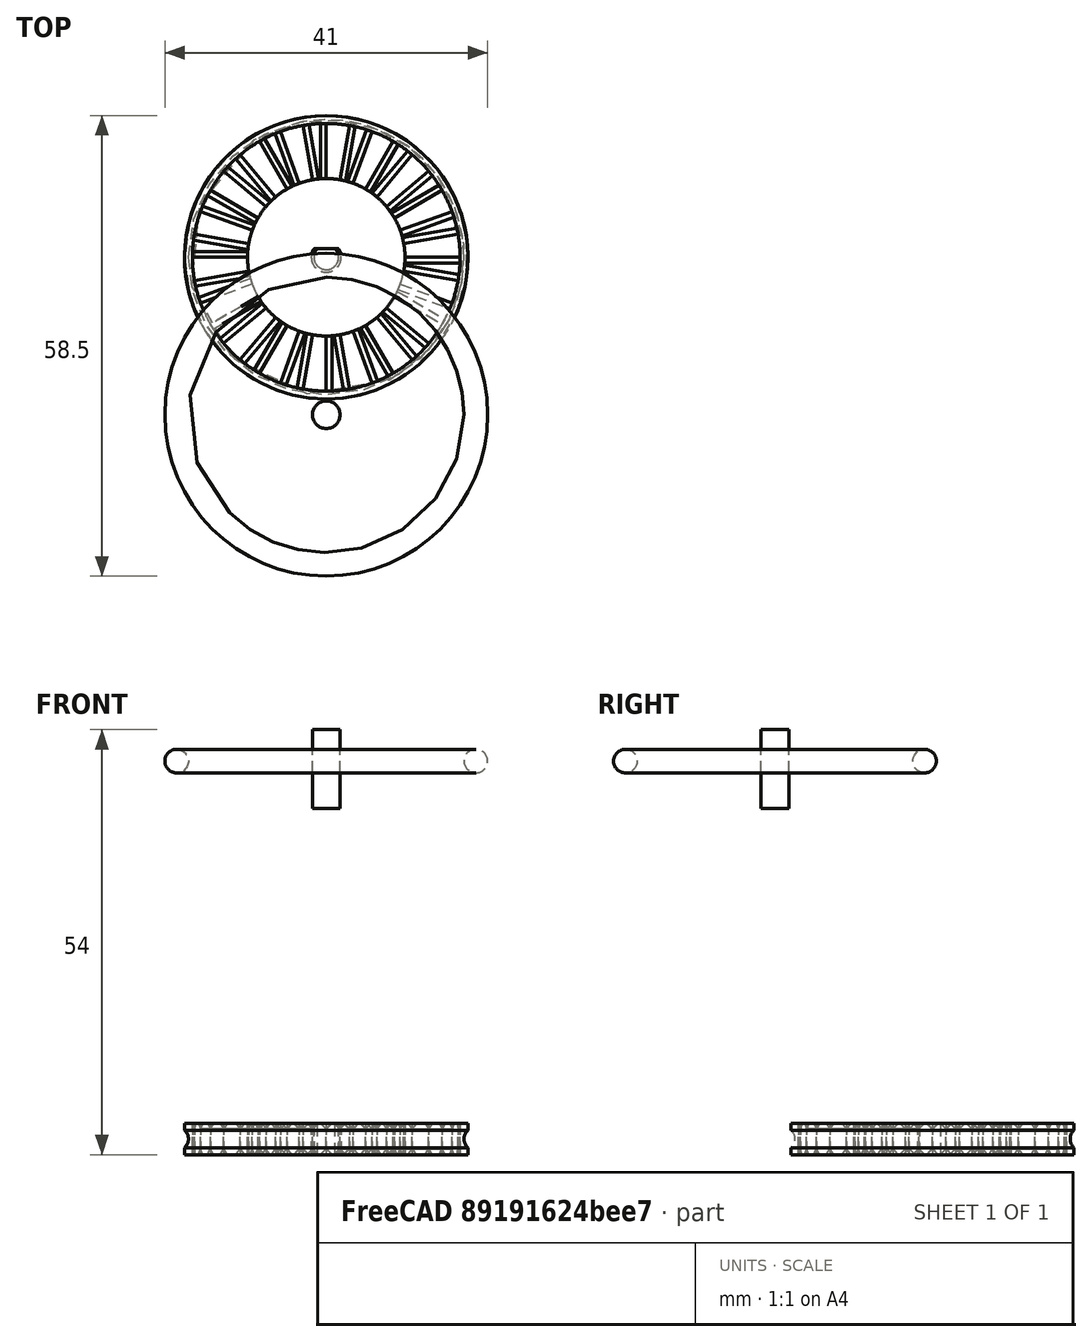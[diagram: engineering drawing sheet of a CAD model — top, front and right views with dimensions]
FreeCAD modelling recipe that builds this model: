
FCSTD DOCUMENT  (FreeCAD 0.17R13522 (Git))
Label: wheel 1.57 hole
License: All rights reserved
LicenseURL: http://en.wikipedia.org/wiki/All_rights_reserved
objects: Part::Feature×34, Part::Cut×13, Part::Cylinder×7, Part::Box×5, Part::Chamfer×4, Part::Torus×3, Part::MultiFuse×2
note: 68 computed .brp shape members not serialized (recipe doc carries the construction recipe); baked Part::Feature solids carry a one-line shape summary decoded from their .brp

FEATURE [Part::Cylinder] Cylinder012  label="wheel1a"
  Angle = 360
  AttacherType = Attacher::AttachEngine3D
  Height = 4
  Radius = 18
FEATURE [Part::Cylinder] Cylinder028  label="Cylinder024"
  Angle = 360
  AttacherType = Attacher::AttachEngine3D
  Height = 10
  Placement = pos=(0,0,-1) rot=(0,0,1;0rad)
  Radius = 1.57
FEATURE [Part::Box] Box084016  label="Cube067"
  AttacherType = Attacher::AttachEngine3D
  Height = 12
  Length = 10
  Placement = pos=(-5,1.1,-1.5) rot=(0,0,1;0rad)
  Width = 10
FEATURE [Part::Cut] Cut057
  Base = -> Cylinder028
  Tool = -> Box084016
FEATURE [Part::Cut] Cut062
  Base = -> Cylinder012
  Tool = -> Cut057
FEATURE [Part::Torus] Torus002
  Angle1 = -180
  Angle2 = 180
  Angle3 = 360
  AttacherType = Attacher::AttachEngine3D
  Placement = pos=(0,0,2) rot=(0,0,1;0rad)
  Radius1 = 19
  Radius2 = 1.5
FEATURE [Part::Cut] Cut063  label="wheel"
  Base = -> Cut062
  Tool = -> Torus002
FEATURE [Part::Torus] Torus
  Angle1 = -180
  Angle2 = 180
  Angle3 = 360
  AttacherType = Attacher::AttachEngine3D
  Placement = pos=(0,-20,50) rot=(0,0,1;0rad)
  Radius1 = 19
  Radius2 = 1.5
FEATURE [Part::Cylinder] Cylinder062  label="Cylinder158"
  Angle = 360
  AttacherType = Attacher::AttachEngine3D
  Height = 10
  Radius = 17
FEATURE [Part::Cylinder] Cylinder063  label="Cylinder159"
  Angle = 360
  AttacherType = Attacher::AttachEngine3D
  Height = 16
  Placement = pos=(0,0,-4) rot=(0,0,1;0rad)
  Radius = 10
FEATURE [Part::Cut] Cut044
  Base = -> Cylinder062
  Tool = -> Cylinder063
FEATURE [Part::Box] Box026  label="Cube025"
  AttacherType = Attacher::AttachEngine3D
  Height = 20
  Length = 18
  Placement = pos=(0,0,-5) rot=(0,0,1;0rad)
  Width = 20
FEATURE [Part::Box] Box027  label="Cube026"
  AttacherType = Attacher::AttachEngine3D
  Height = 20
  Length = 10
  Placement = pos=(0,0,-5) rot=(0,0,1;0.174533rad)
  Width = 20
FEATURE [Part::Cut] Cut045
  Base = -> Box027
  Tool = -> Box026
FEATURE [Part::Feature] Cut045001
  Placement = pos=(0,0,0) rot=(0,0,1;0.349066rad)
  shape: bbox 10 x 22.32 x 20 mm, 7 faces (baked)
FEATURE [Part::Feature] Cut045002
  Placement = pos=(0,0,0) rot=(0,0,1;0.698132rad)
  shape: bbox 15.32 x 20.52 x 20 mm, 7 faces (baked)
FEATURE [Part::Feature] Cut045003
  Placement = pos=(0,0,0) rot=(0,0,1;1.0472rad)
  shape: bbox 18.79 x 16.24 x 20 mm, 7 faces (baked)
FEATURE [Part::Feature] Cut045004
  Placement = pos=(0,0,0) rot=(0,0,1;1.39626rad)
  shape: bbox 20 x 10 x 20 mm, 7 faces (baked)
FEATURE [Part::Feature] Cut045005
  Placement = pos=(0,0,0) rot=(0,0,1;1.74533rad)
  shape: bbox 22.21 x 9.894 x 20 mm, 7 faces (baked)
FEATURE [Part::Feature] Cut045006
  Placement = pos=(0,0,0) rot=(0,0,1;2.0944rad)
  shape: bbox 21.75 x 12.86 x 20 mm, 7 faces (baked)
FEATURE [Part::Feature] Cut045007
  Placement = pos=(0,0,0) rot=(0,0,1;2.44346rad)
  shape: bbox 18.66 x 17.32 x 20 mm, 7 faces (baked)
FEATURE [Part::Feature] Cut045008
  Placement = pos=(0,0,0) rot=(0,0,1;2.79253rad)
  shape: bbox 13.32 x 19.7 x 20 mm, 7 faces (baked)
FEATURE [Part::Feature] Cut045009
  Placement = pos=(0,0,0) rot=(0,0,1;3.14159rad)
  shape: bbox 10.1 x 21.43 x 20 mm, 7 faces (baked)
FEATURE [Part::Feature] Cut045010
  Placement = pos=(0,0,0) rot=(0,0,1;3.49066rad)
  shape: bbox 10 x 22.32 x 20 mm, 7 faces (baked)
FEATURE [Part::Feature] Cut045011
  Placement = pos=(0,0,0) rot=(0,0,1;3.83972rad)
  shape: bbox 15.32 x 20.52 x 20 mm, 7 faces (baked)
FEATURE [Part::Feature] Cut045012
  Placement = pos=(0,0,0) rot=(0,0,1;4.18879rad)
  shape: bbox 18.79 x 16.24 x 20 mm, 7 faces (baked)
FEATURE [Part::Feature] Cut045013
  Placement = pos=(0,0,0) rot=(0,0,-1;1.74533rad)
  shape: bbox 20 x 10 x 20 mm, 7 faces (baked)
FEATURE [Part::Feature] Cut045014
  Placement = pos=(0,0,0) rot=(0,0,-1;1.39626rad)
  shape: bbox 22.21 x 9.894 x 20 mm, 7 faces (baked)
FEATURE [Part::Feature] Cut045015
  Placement = pos=(0,0,0) rot=(0,0,-1;1.0472rad)
  shape: bbox 21.75 x 12.86 x 20 mm, 7 faces (baked)
FEATURE [Part::Feature] Cut045016
  Placement = pos=(0,0,0) rot=(0,0,-1;0.698132rad)
  shape: bbox 18.66 x 17.32 x 20 mm, 7 faces (baked)
FEATURE [Part::Feature] Cut045017
  Placement = pos=(0,0,0) rot=(0,0,-1;0.349066rad)
  shape: bbox 13.32 x 19.7 x 20 mm, 7 faces (baked)
FEATURE [Part::MultiFuse] Fusion095
  Shapes = -> [Cut045001,Cut045008,Cut045010,Cut045009,Cut045005,Cut045003,Cut045006,Cut045002,Cut045004,Cut045007,Cut045016,Cut045017,Cut045011,Cut045012,Cut045013,Cut045014,Cut045015,Cut045]
FEATURE [Part::Cut] Cut045018
  Base = -> Cut044
  Placement = pos=(0,0,-1) rot=(0,1,0;0rad)
  Tool = -> Fusion095
FEATURE [Part::Cylinder] Cylinder064  label="Cylinder160"
  Angle = 360
  AttacherType = Attacher::AttachEngine3D
  Height = 10
  Placement = pos=(0,-20,44) rot=(0,0,1;0rad)
  Radius = 1.75
FEATURE [Part::Cut] Cut
  Base = -> Cut063
  Tool = -> Cut045018
FEATURE [Part::Cut] Cut008
FEATURE [Part::Torus] Torus001
  Angle1 = -180
  Angle2 = 180
  Angle3 = 360
  AttacherType = Attacher::AttachEngine3D
  Placement = pos=(0,0,2) rot=(0,0,1;0rad)
  Radius1 = 19
  Radius2 = 1.5
FEATURE [Part::Cut] Cut009  label="wheel2"
  Base = -> Cut008
  Placement = pos=(75,-7,15) rot=(0,1,0;1.5708rad)
  Tool = -> Torus001
FEATURE [Part::Cylinder] Cylinder065  label="Cylinder161"
  Angle = 360
  AttacherType = Attacher::AttachEngine3D
  Height = 10
  Radius = 17
FEATURE [Part::Cylinder] Cylinder066  label="Cylinder162"
  Angle = 360
  AttacherType = Attacher::AttachEngine3D
  Height = 16
  Placement = pos=(0,0,-4) rot=(0,0,1;0rad)
  Radius = 10
FEATURE [Part::Cut] Cut045019
  Base = -> Cylinder065
  Tool = -> Cylinder066
FEATURE [Part::Box] Box084017  label="Cube068"
  AttacherType = Attacher::AttachEngine3D
  Height = 20
  Length = 18
  Placement = pos=(0,0,-5) rot=(0,0,1;0rad)
  Width = 20
FEATURE [Part::Box] Box084018  label="Cube069"
  AttacherType = Attacher::AttachEngine3D
  Height = 20
  Length = 10
  Placement = pos=(0,0,-5) rot=(0,0,1;0.174533rad)
  Width = 20
FEATURE [Part::Cut] Cut045020
  Base = -> Box084018
  Tool = -> Box084017
FEATURE [Part::Feature] Cut045021
  Placement = pos=(0,0,0) rot=(0,0,1;0.349066rad)
  shape: bbox 10 x 22.32 x 20 mm, 7 faces (baked)
FEATURE [Part::Feature] Cut045022
  Placement = pos=(0,0,0) rot=(0,0,1;0.698132rad)
  shape: bbox 15.32 x 20.52 x 20 mm, 7 faces (baked)
FEATURE [Part::Feature] Cut045023
  Placement = pos=(0,0,0) rot=(0,0,1;1.0472rad)
  shape: bbox 18.79 x 16.24 x 20 mm, 7 faces (baked)
FEATURE [Part::Feature] Cut045024
  Placement = pos=(0,0,0) rot=(0,0,1;1.39626rad)
  shape: bbox 20 x 10 x 20 mm, 7 faces (baked)
FEATURE [Part::Feature] Cut045025
  Placement = pos=(0,0,0) rot=(0,0,1;1.74533rad)
  shape: bbox 22.21 x 9.894 x 20 mm, 7 faces (baked)
FEATURE [Part::Feature] Cut045026
  Placement = pos=(0,0,0) rot=(0,0,1;2.0944rad)
  shape: bbox 21.75 x 12.86 x 20 mm, 7 faces (baked)
FEATURE [Part::Feature] Cut045027
  Placement = pos=(0,0,0) rot=(0,0,1;2.44346rad)
  shape: bbox 18.66 x 17.32 x 20 mm, 7 faces (baked)
FEATURE [Part::Feature] Cut045028
  Placement = pos=(0,0,0) rot=(0,0,1;2.79253rad)
  shape: bbox 13.32 x 19.7 x 20 mm, 7 faces (baked)
FEATURE [Part::Feature] Cut045029
  Placement = pos=(0,0,0) rot=(0,0,1;3.14159rad)
  shape: bbox 10.1 x 21.43 x 20 mm, 7 faces (baked)
FEATURE [Part::Feature] Cut045030
  Placement = pos=(0,0,0) rot=(0,0,1;3.49066rad)
  shape: bbox 10 x 22.32 x 20 mm, 7 faces (baked)
FEATURE [Part::Feature] Cut045031
  Placement = pos=(0,0,0) rot=(0,0,1;3.83972rad)
  shape: bbox 15.32 x 20.52 x 20 mm, 7 faces (baked)
FEATURE [Part::Feature] Cut045032
  Placement = pos=(0,0,0) rot=(0,0,1;4.18879rad)
  shape: bbox 18.79 x 16.24 x 20 mm, 7 faces (baked)
FEATURE [Part::Feature] Cut045033
  Placement = pos=(0,0,0) rot=(0,0,-1;1.74533rad)
  shape: bbox 20 x 10 x 20 mm, 7 faces (baked)
FEATURE [Part::Feature] Cut045034
  Placement = pos=(0,0,0) rot=(0,0,-1;1.39626rad)
  shape: bbox 22.21 x 9.894 x 20 mm, 7 faces (baked)
FEATURE [Part::Feature] Cut045035
  Placement = pos=(0,0,0) rot=(0,0,-1;1.0472rad)
  shape: bbox 21.75 x 12.86 x 20 mm, 7 faces (baked)
FEATURE [Part::Feature] Cut045036
  Placement = pos=(0,0,0) rot=(0,0,-1;0.698132rad)
  shape: bbox 18.66 x 17.32 x 20 mm, 7 faces (baked)
FEATURE [Part::Feature] Cut045037
  Placement = pos=(0,0,0) rot=(0,0,-1;0.349066rad)
  shape: bbox 13.32 x 19.7 x 20 mm, 7 faces (baked)
FEATURE [Part::MultiFuse] Fusion096
  Shapes = -> [Cut045021,Cut045028,Cut045030,Cut045029,Cut045025,Cut045023,Cut045026,Cut045022,Cut045024,Cut045027,Cut045036,Cut045037,Cut045031,Cut045032,Cut045033,Cut045034,Cut045035,Cut045020]
FEATURE [Part::Cut] Cut045038
  Base = -> Cut045019
  Placement = pos=(72,-7,15) rot=(0,1,0;1.5708rad)
  Tool = -> Fusion096
FEATURE [Part::Cut] Cut045039  label="Wheel with Spokes AB"
  Base = -> Cut009
  Placement = pos=(-15,7,79) rot=(0,1,0;1.5708rad)
  Tool = -> Cut045038
FEATURE [Part::Chamfer] Chamfer
  Base = -> Cut
  Edges = 14 edges r=0.75: [Edge27,Edge50,Edge52,Edge56,Edge62,Edge64,Edge66,Edge68,Edge70,Edge72,Edge74,Edge76,Edge78,Edge80]
FEATURE [Part::Chamfer] Chamfer001
  Base = -> Chamfer
  Edges = 22 edges r=0.75: [Edge4,Edge9,Edge11,Edge13,Edge15,Edge17,Edge19,Edge21,Edge23,Edge25,Edge27,Edge32,Edge34,Edge36,Edge38,Edge40,Edge42,Edge44,Edge46,Edge48,Edge50,Edge62]
FEATURE [Part::Chamfer] Chamfer002
  Base = -> Chamfer001
  Edges = 14 edges r=0.75: [Edge382,Edge383,Edge384,Edge394,Edge395,Edge396,Edge397,Edge398,Edge399,Edge400,Edge401,Edge406,Edge407,Edge408]
FEATURE [Part::Chamfer] Chamfer003
  Base = -> Chamfer002
  Edges = 22 edges r=0.75: [Edge23,Edge28,Edge30,Edge32,Edge34,Edge36,Edge38,Edge40,Edge42,Edge47,Edge49,Edge51,Edge53,Edge55,Edge57,Edge59,Edge61,Edge63,Edge65,Edge67,Edge69,Edge117]
